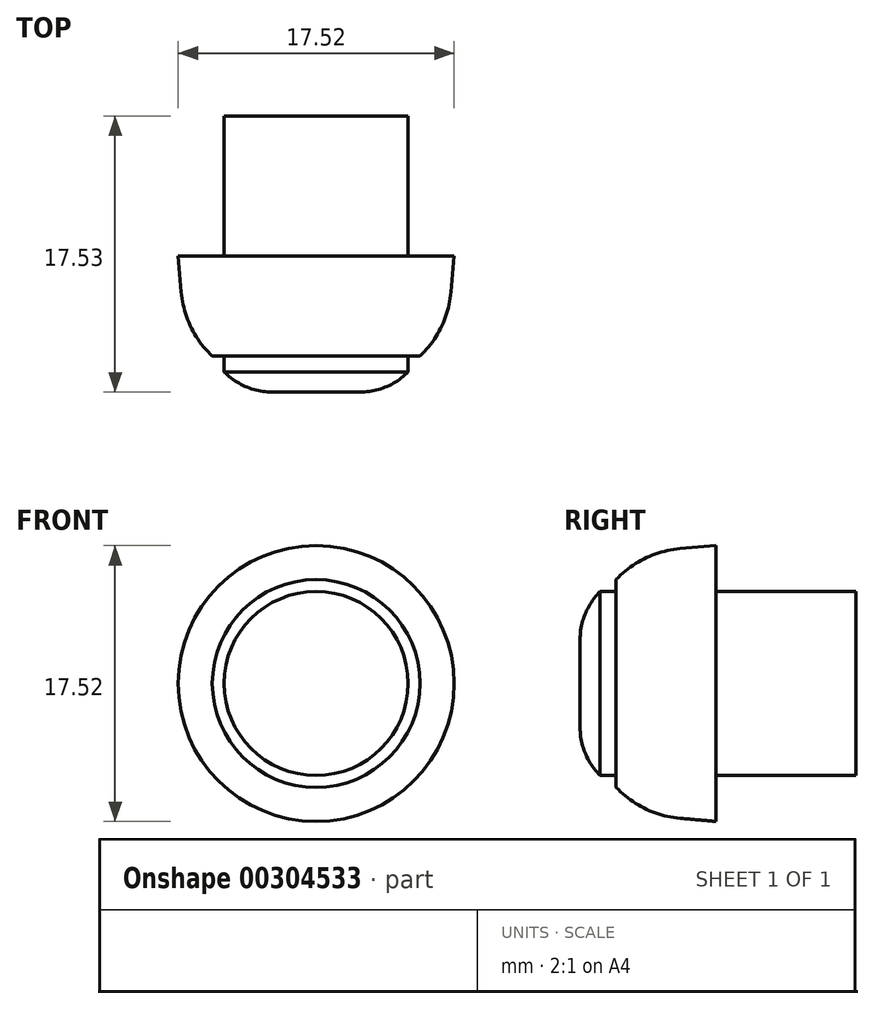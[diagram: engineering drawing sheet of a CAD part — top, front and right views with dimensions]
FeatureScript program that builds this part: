
annotation { "Feature Type Name" : "Feature", "Feature Type Description" : "" }
export const myFeature = defineFeature(function(context is Context, id is Id, definition is map)
    precondition{}
    {
        {
            var Q0;
            Q0=qCreatedBy(makeId("Right.planeOp"),FACE);
            var sketch = newSketch(context, id + "F0", { "sketchPlane" : qUnion([Q0])});
            skLineSegment(sketch, "E0", {"start": v(-24.78, 0) * mm, "end": v(44.61, 0) * mm, "construction": true});
            skLineSegment(sketch, "E1", {"start": v(8.9, 0) * mm, "end": v(8.9, 5.84) * mm});
            skLineSegment(sketch, "E2", {"start": v(8.9, 5.84) * mm, "end": v(0, 5.84) * mm});
            skLineSegment(sketch, "E3", {"start": v(0, 5.84) * mm, "end": v(0, 8.76) * mm});
            skLineSegment(sketch, "E4", {"start": v(0, 8.76) * mm, "end": v(-2.29, 8.56) * mm});
            skArc(sketch, "E5", {"start": v(-2.29, 8.56) * mm, "mid": v(-4.5, 7.95) * mm, "end": v(-6.35, 6.6) * mm});
            skLineSegment(sketch, "E6", {"start": v(-6.35, 6.6) * mm, "end": v(-6.35, 5.84) * mm});
            skLineSegment(sketch, "E7", {"start": v(-6.35, 5.84) * mm, "end": v(-7.37, 5.84) * mm});
            skLineSegment(sketch, "E8", {"start": v(8.9, 0) * mm, "end": v(-8.64, 0) * mm});
            skLineSegment(sketch, "E9", {"start": v(-8.64, 0) * mm, "end": v(-8.64, 2.8) * mm});
            skArc(sketch, "E10", {"start": v(-7.37, 5.84) * mm, "mid": v(-8.3, 4.44) * mm, "end": v(-8.64, 2.8) * mm});
            skSolve(sketch);
        }
        {
            var Q0;
            Q0 = qSketchRegion(id + "F0", true);
            var Q1;
            Q1=sQuery(id+"F0.wireOp",EDGE,"E0");
            revolve(context, id + "F1", {"entities" : qUnion([Q0]), "axis" : qUnion([Q1]), "revolveType" : RevolveType.FULL});
        }
    });
